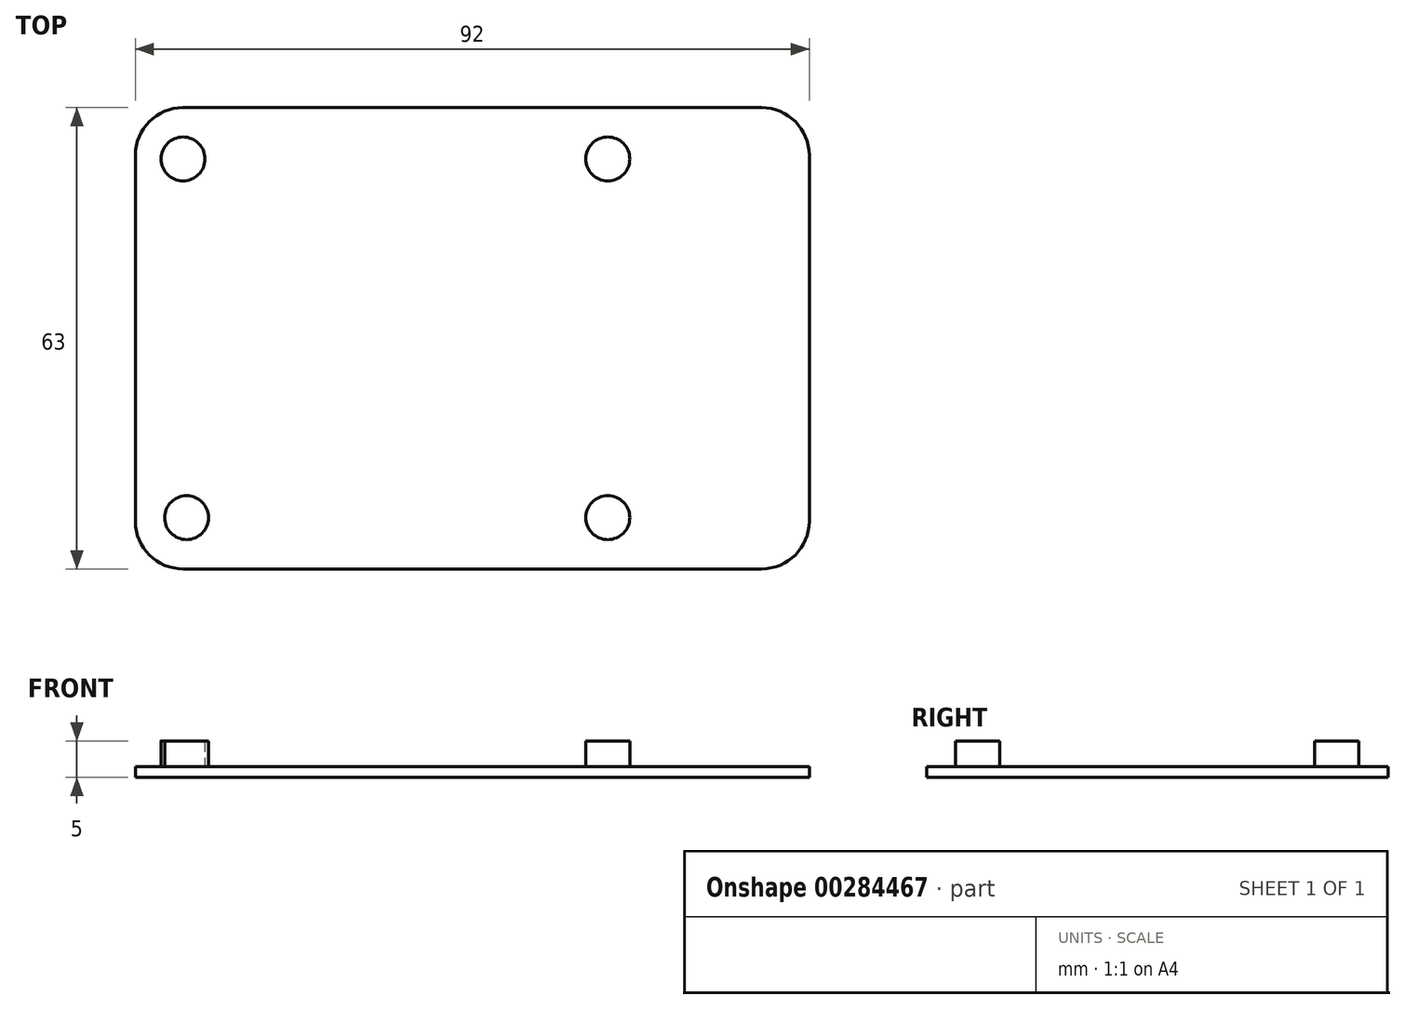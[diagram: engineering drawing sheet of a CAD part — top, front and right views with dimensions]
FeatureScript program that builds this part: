
annotation { "Feature Type Name" : "Feature", "Feature Type Description" : "" }
export const myFeature = defineFeature(function(context is Context, id is Id, definition is map)
    precondition{}
    {
        {
            assignVariable(context, id + "F0", {"name" : "shell", "anyValue" : 1.5});
        }
        {
            var Q0;
            Q0=qCreatedBy(makeId("Top.planeOp"),FACE);
            var sketch = newSketch(context, id + "F1", { "sketchPlane" : qUnion([Q0])});
            skLineSegment(sketch, "E0.bottom", {"start": v(-39.5, 28) * mm, "end": v(39.5, 28) * mm, "construction": true});
            skLineSegment(sketch, "E0.top", {"start": v(-39.5, -28) * mm, "end": v(39.5, -28) * mm, "construction": true});
            skLineSegment(sketch, "E0.left", {"start": v(-42.5, 25) * mm, "end": v(-42.5, -25) * mm, "construction": true});
            skLineSegment(sketch, "E0.right", {"start": v(42.5, 25) * mm, "end": v(42.5, -25) * mm, "construction": true});
            skPoint(sketch, "E1.visualSharp", {"position": v(-42.5, 28) * mm});
            skArc(sketch, "E1.filletArc", {"start": v(-39.5, 28) * mm, "mid": v(-41.62, 27.12) * mm, "end": v(-42.5, 25) * mm, "construction": true});
            skPoint(sketch, "E2.visualSharp", {"position": v(-42.5, -28) * mm});
            skArc(sketch, "E2.filletArc", {"start": v(-42.5, -25) * mm, "mid": v(-41.62, -27.12) * mm, "end": v(-39.5, -28) * mm, "construction": true});
            skPoint(sketch, "E3.visualSharp", {"position": v(42.5, -28) * mm});
            skArc(sketch, "E3.filletArc", {"start": v(39.5, -28) * mm, "mid": v(41.62, -27.12) * mm, "end": v(42.5, -25) * mm, "construction": true});
            skPoint(sketch, "E4.visualSharp", {"position": v(42.5, 28) * mm});
            skArc(sketch, "E4.filletArc", {"start": v(42.5, 25) * mm, "mid": v(41.62, 27.12) * mm, "end": v(39.5, 28) * mm, "construction": true});
            skCircle(sketch, "E5", {"center": v(-39, -24.5) * mm, "radius": 1.4 * mm, "construction": true});
            skCircle(sketch, "E6", {"center": v(18.5, 24.5) * mm, "radius": 1.4 * mm, "construction": true});
            skCircle(sketch, "E7", {"center": v(18.5, -24.5) * mm, "radius": 1.4 * mm, "construction": true});
            skCircle(sketch, "E8", {"center": v(-39.5, 24.5) * mm, "radius": 1.4 * mm, "construction": true});
            skLineSegment(sketch, "E9.bottom", {"start": v(26.8, 25.6) * mm, "end": v(44.5, 25.6) * mm, "construction": true});
            skLineSegment(sketch, "E9.top", {"start": v(26.8, 12.4) * mm, "end": v(44.5, 12.4) * mm, "construction": true});
            skLineSegment(sketch, "E9.left", {"start": v(26.8, 25.6) * mm, "end": v(26.8, 12.4) * mm, "construction": true});
            skLineSegment(sketch, "E9.right", {"start": v(44.5, 25.6) * mm, "end": v(44.5, 12.4) * mm});
            skLineSegment(sketch, "E10.bottom", {"start": v(44.5, 7.6) * mm, "end": v(26.8, 7.6) * mm, "construction": true});
            skLineSegment(sketch, "E10.top", {"start": v(44.5, -5.6) * mm, "end": v(26.8, -5.6) * mm, "construction": true});
            skLineSegment(sketch, "E10.left", {"start": v(44.5, 7.6) * mm, "end": v(44.5, -5.6) * mm, "construction": true});
            skLineSegment(sketch, "E10.right", {"start": v(26.8, 7.6) * mm, "end": v(26.8, -5.6) * mm, "construction": true});
            skLineSegment(sketch, "E11.bottom", {"start": v(44.5, -25.3) * mm, "end": v(26.8, -25.3) * mm, "construction": true});
            skLineSegment(sketch, "E11.top", {"start": v(44.5, -9.7) * mm, "end": v(26.8, -9.7) * mm, "construction": true});
            skLineSegment(sketch, "E11.left", {"start": v(44.5, -9.7) * mm, "end": v(44.5, -25.3) * mm, "construction": true});
            skLineSegment(sketch, "E11.right", {"start": v(26.8, -9.7) * mm, "end": v(26.8, -25.3) * mm, "construction": true});
            skPoint(sketch, "E12", {"position": v(44.5, 19) * mm});
            skPoint(sketch, "E13", {"position": v(44.5, 1) * mm});
            skPoint(sketch, "E14", {"position": v(44.5, -17.5) * mm});
            skLineSegment(sketch, "E15.bottom", {"start": v(-35.9, 27) * mm, "end": v(14.9, 27) * mm, "construction": true});
            skLineSegment(sketch, "E15.top", {"start": v(-35.9, 22) * mm, "end": v(14.9, 22) * mm, "construction": true});
            skLineSegment(sketch, "E15.left", {"start": v(-35.9, 27) * mm, "end": v(-35.9, 22) * mm, "construction": true});
            skLineSegment(sketch, "E15.right", {"start": v(14.9, 27) * mm, "end": v(14.9, 22) * mm, "construction": true});
            skPoint(sketch, "E16", {"position": v(-10.5, 27) * mm});
            skPoint(sketch, "E17", {"position": v(-35.9, 24.5) * mm});
            skArc(sketch, "E18.0", {"start": v(-39.5, 31.5) * mm, "mid": v(-44.1, 29.6) * mm, "end": v(-46, 25) * mm});
            skLineSegment(sketch, "E18.1", {"start": v(-39.5, 31.5) * mm, "end": v(39.5, 31.5) * mm});
            skLineSegment(sketch, "E18.2", {"start": v(-46, 25) * mm, "end": v(-46, -25) * mm});
            skArc(sketch, "E18.3", {"start": v(46, 25) * mm, "mid": v(44.1, 29.6) * mm, "end": v(39.5, 31.5) * mm});
            skArc(sketch, "E18.4", {"start": v(-46, -25) * mm, "mid": v(-44.1, -29.6) * mm, "end": v(-39.5, -31.5) * mm});
            skLineSegment(sketch, "E18.5", {"start": v(-39.5, -31.5) * mm, "end": v(39.5, -31.5) * mm});
            skArc(sketch, "E18.6", {"start": v(39.5, -31.5) * mm, "mid": v(44.1, -29.6) * mm, "end": v(46, -25) * mm});
            skLineSegment(sketch, "E18.7", {"start": v(46, 25) * mm, "end": v(46, -25) * mm});
            skSolve(sketch);
        }
        {
            var Q0;
            Q0 = qSketchRegion(id + "F1", true);
            extrude(context, id + "F2", {"entities" : qUnion([Q0]), "depth" : (getVariable(context, 'shell')) * mm});
        }
        {
            var Q0;
            Q0=makeQuery(id+"F2.opExtrude","CAP_FACE",FACE,{"disambiguationData":[OSD([sQuery(id+"F1.wireOp",EDGE,"E18.0"),sQuery(id+"F1.wireOp",EDGE,"E18.1"),sQuery(id+"F1.wireOp",EDGE,"E18.2"),sQuery(id+"F1.wireOp",EDGE,"E18.3"),sQuery(id+"F1.wireOp",EDGE,"E18.4"),sQuery(id+"F1.wireOp",EDGE,"E18.5"),sQuery(id+"F1.wireOp",EDGE,"E18.6"),sQuery(id+"F1.wireOp",EDGE,"E18.7")])],"isStart":false});
            var sketch = newSketch(context, id + "F3", { "sketchPlane" : qUnion([Q0])});
            skCircle(sketch, "E19", {"center": v(-39.5, 24.5) * mm, "radius": 3 * mm});
            skCircle(sketch, "E20", {"center": v(18.5, 24.5) * mm, "radius": 3 * mm});
            skCircle(sketch, "E21", {"center": v(-39, -24.5) * mm, "radius": 3 * mm});
            skCircle(sketch, "E22", {"center": v(18.5, -24.5) * mm, "radius": 3 * mm});
            skSolve(sketch);
        }
        {
            var Q0;
            Q0=qCreatedBy(makeId("Top.planeOp"),FACE);
            cPlane(context, id + "F4", {"entities" : qUnion([Q0]), "cplaneType" : CPlaneType.OFFSET, "offset" : 5 * mm, "width" : 150 * mm, "height" : 150 * mm});
        }
        {
            var Q0;
            Q0 = qSketchRegion(id + "F3", true);
            var Q1;
            Q1=qCreatedBy(id+"F4.planeOp",FACE);
            extrude(context, id + "F5", {"entities" : qUnion([Q0]), "operationType" : NewBodyOperationType.ADD, "endBound" : BoundingType.UP_TO_SURFACE, "endBoundEntityFace" : qUnion([Q1]), "depth" : 5 * mm});
        }
    });
